# Revit family: Deckel_Bogen_90_Russia
name_source: partatom
category: Generic Models
revit_build: Autodesk Revit 2015 (Build: 20140606_1530(x64)
units: mm (PartAtom-declared; Revit-internal decimal feet)

## types (7) — shared parameters
Manufacturer = OBO Bettermann
Material = Steel, Galvanized
URL = http://www.obo-bettermann.com

## per-type parameters (varying)
| type | A | Article Type | GTIN | Manufacturer Art. No. |
| DFB 90 100 FS RU | 152 mm  [stored 0.498688 ft] | DFB 90 100 FS RU | 4012196606320 | 7129741 |
| DFB 90 150 FS RU | 202 mm  [stored 0.66273 ft] | DFF 90 150 FS RU | 4012196649457 | 7129742 |
| DFB 90 200 FS RU | 252 mm  [stored 0.826772 ft] | DFF 90 200 FS RU | 4012196606337 | 7129743 |
| DFB 90 300 FS RU | 352 mm  [stored 1.15486 ft] | DFB 90 300 FS RU | 4012196606344 | 7129745 |
| DFB 90 400 FS RU | 452 mm  [stored 1.48294 ft] | DFB 90 400 FS RU | 4012196626359 | 71249747 |
| DFB 90 500 FS RU | 552 mm  [stored 1.81102 ft] | DFB 90 500 FS RU | 4012196626366 | 7129749 |
| DFB 90 600 FS RU | 652 mm  [stored 2.13911 ft] | DFB 90 600 FS RU | 4012196626373 | 7129751 |

note: [stored X ft] marks values corroborated as IEEE doubles in the binary element streams (Revit-internal decimal feet)

## geometry (parser evidence)
native form markers: Sweep x2
no freeform markers — native parametric forms only
